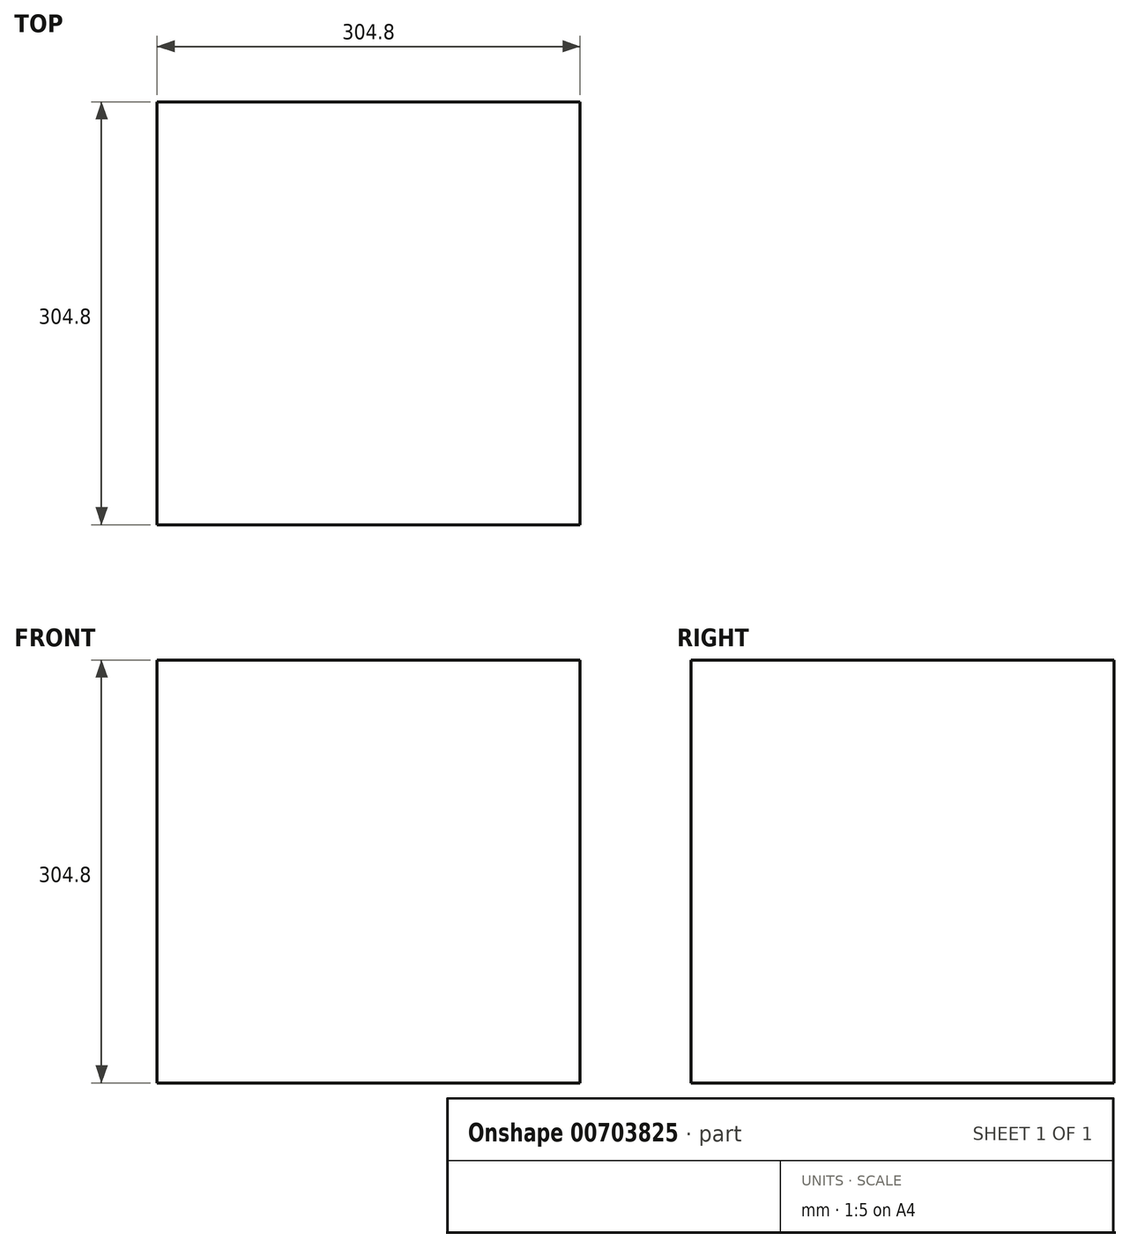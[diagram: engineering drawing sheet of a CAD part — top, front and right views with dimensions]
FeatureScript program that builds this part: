
annotation { "Feature Type Name" : "Feature", "Feature Type Description" : "" }
export const myFeature = defineFeature(function(context is Context, id is Id, definition is map)
    precondition{}
    {
        {
            var Q0;
            Q0=qCreatedBy(makeId("Top.planeOp"),FACE);
            var sketch = newSketch(context, id + "F0", { "sketchPlane" : qUnion([Q0])});
            skLineSegment(sketch, "E0.bottom", {"start": v(152.4, -152.4) * mm, "end": v(-152.4, -152.4) * mm});
            skLineSegment(sketch, "E0.top", {"start": v(152.4, 152.4) * mm, "end": v(-152.4, 152.4) * mm});
            skLineSegment(sketch, "E0.left", {"start": v(152.4, -152.4) * mm, "end": v(152.4, 152.4) * mm});
            skLineSegment(sketch, "E0.right", {"start": v(-152.4, -152.4) * mm, "end": v(-152.4, 152.4) * mm});
            skPoint(sketch, "E0.middle", {"position": v(0, 0) * mm});
            skSolve(sketch);
        }
        {
            var Q0;
            Q0 = qSketchRegion(id + "F0", true);
            extrude(context, id + "F1", {"entities" : qUnion([Q0]), "depth" : 304.8 * mm, "offsetDistance" : 25.4 * mm});
        }
    });
